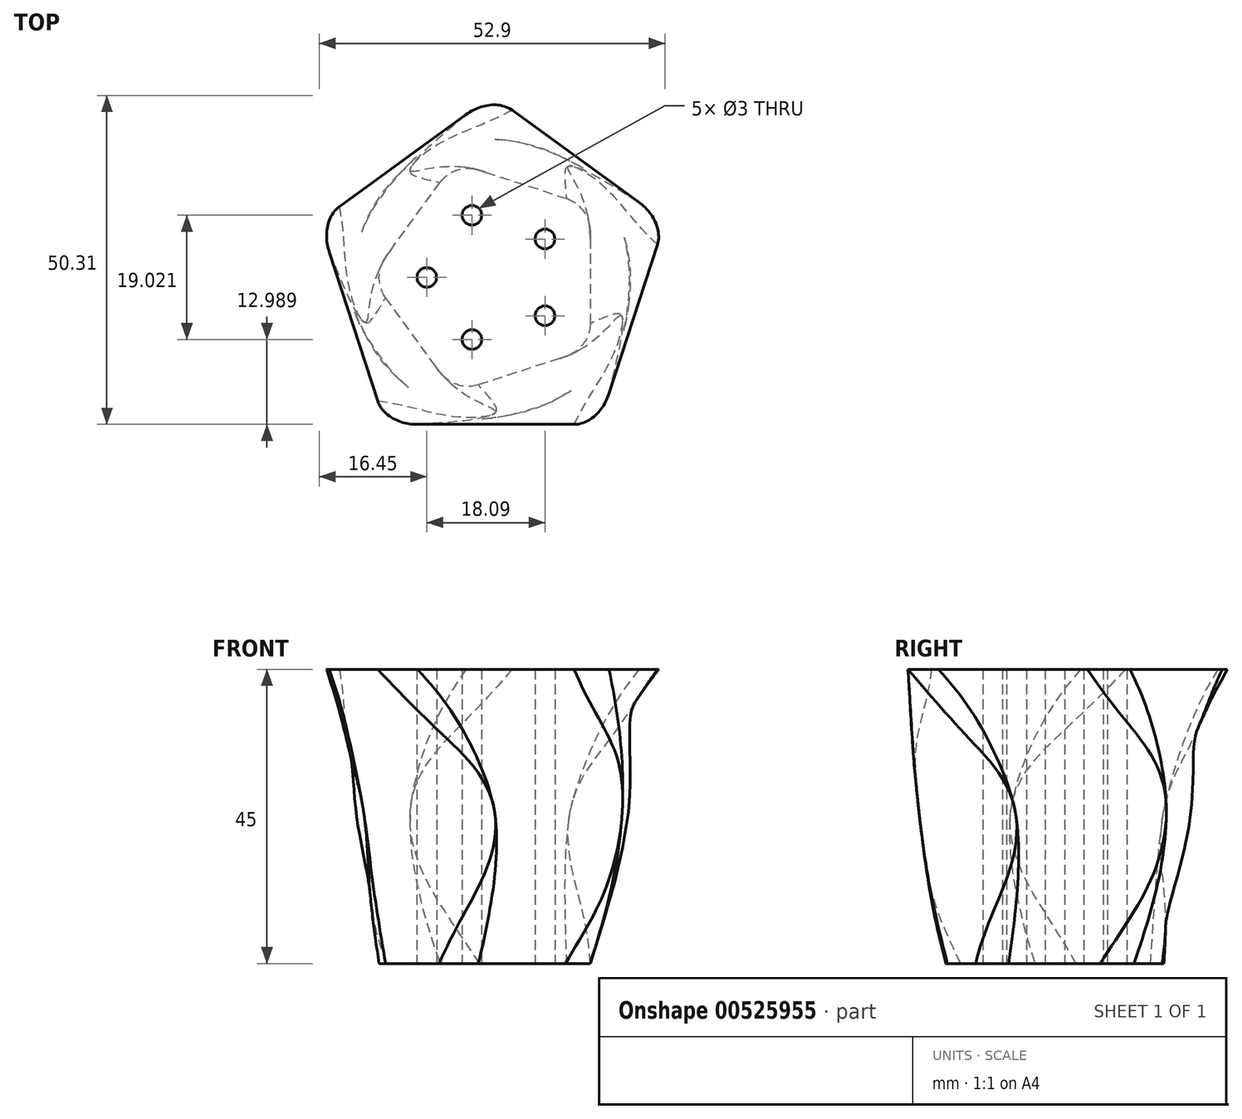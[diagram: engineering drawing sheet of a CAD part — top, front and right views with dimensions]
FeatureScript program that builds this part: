
annotation { "Feature Type Name" : "Feature", "Feature Type Description" : "" }
export const myFeature = defineFeature(function(context is Context, id is Id, definition is map)
    precondition{}
    {
        {
            var Q0;
            Q0=qCreatedBy(makeId("Top.planeOp"),FACE);
            var sketch = newSketch(context, id + "F0", { "sketchPlane" : qUnion([Q0])});
            skCircle(sketch, "E0.cCircle", {"center": v(0, 0) * mm, "radius": 15 * mm, "construction": true});
            skLineSegment(sketch, "E0.0", {"start": v(15, 10.9) * mm, "end": v(15, -10.9) * mm});
            skLineSegment(sketch, "E0.1", {"start": v(15, -10.9) * mm, "end": v(-5.73, -17.63) * mm});
            skLineSegment(sketch, "E0.2", {"start": v(-5.73, -17.63) * mm, "end": v(-18.54, 0) * mm});
            skLineSegment(sketch, "E0.3", {"start": v(-18.54, 0) * mm, "end": v(-5.73, 17.63) * mm});
            skLineSegment(sketch, "E0.4", {"start": v(-5.73, 17.63) * mm, "end": v(15, 10.9) * mm});
            skPoint(sketch, "E0.0.midPoint", {"position": v(15, 0) * mm});
            skSolve(sketch);
        }
        {
            var Q0;
            Q0=qCreatedBy(makeId("Top.planeOp"),FACE);
            cPlane(context, id + "F1", {"entities" : qUnion([Q0]), "cplaneType" : CPlaneType.OFFSET, "offset" : 25 * mm, "width" : 150 * mm, "height" : 150 * mm});
        }
        {
            var Q0;
            Q0=qCreatedBy(id+"F1.planeOp",FACE);
            var sketch = newSketch(context, id + "F2", { "sketchPlane" : qUnion([Q0])});
            skLineSegment(sketch, "E1.0", {"start": v(0, -21) * mm, "end": v(-19.97, -6.49) * mm, "construction": true});
            skLineSegment(sketch, "E1.1", {"start": v(-19.97, -6.49) * mm, "end": v(-12.34, 16.99) * mm, "construction": true});
            skLineSegment(sketch, "E1.2", {"start": v(-12.34, 16.99) * mm, "end": v(12.34, 16.99) * mm, "construction": true});
            skLineSegment(sketch, "E1.3", {"start": v(12.34, 16.99) * mm, "end": v(19.97, -6.49) * mm, "construction": true});
            skLineSegment(sketch, "E1.4", {"start": v(19.97, -6.49) * mm, "end": v(0, -21) * mm, "construction": true});
            skArc(sketch, "E2", {"start": v(19.97, -6.49) * mm, "mid": v(19.97, 6.49) * mm, "end": v(12.34, 16.99) * mm});
            skArc(sketch, "E3", {"start": v(0, -21) * mm, "mid": v(12.34, -16.99) * mm, "end": v(19.97, -6.49) * mm});
            skArc(sketch, "E4", {"start": v(-19.97, -6.49) * mm, "mid": v(-12.34, -16.99) * mm, "end": v(0, -21) * mm});
            skArc(sketch, "E5", {"start": v(-12.34, 16.99) * mm, "mid": v(-19.97, 6.49) * mm, "end": v(-19.97, -6.49) * mm});
            skArc(sketch, "E6", {"start": v(12.34, 16.99) * mm, "mid": v(0, 21) * mm, "end": v(-12.34, 16.99) * mm});
            skSolve(sketch);
        }
        {
            var Q0;
            Q0=qCreatedBy(id+"F1.planeOp",FACE);
            cPlane(context, id + "F3", {"entities" : qUnion([Q0]), "cplaneType" : CPlaneType.OFFSET, "offset" : 20 * mm, "width" : 150 * mm, "height" : 150 * mm});
        }
        {
            var Q0;
            Q0=qCreatedBy(id+"F3.planeOp",FACE);
            var sketch = newSketch(context, id + "F4", { "sketchPlane" : qUnion([Q0])});
            skCircle(sketch, "E7.cCircle", {"center": v(0, 0) * mm, "radius": 22.5 * mm, "construction": true});
            skLineSegment(sketch, "E7.0", {"start": v(16.35, -22.5) * mm, "end": v(-16.35, -22.5) * mm});
            skLineSegment(sketch, "E7.1", {"start": v(-16.35, -22.5) * mm, "end": v(-26.45, 8.6) * mm});
            skLineSegment(sketch, "E7.2", {"start": v(-26.45, 8.6) * mm, "end": v(0, 27.81) * mm});
            skLineSegment(sketch, "E7.3", {"start": v(0, 27.81) * mm, "end": v(26.45, 8.6) * mm});
            skLineSegment(sketch, "E7.4", {"start": v(26.45, 8.6) * mm, "end": v(16.35, -22.5) * mm});
            skPoint(sketch, "E7.0.midPoint", {"position": v(0, -22.5) * mm});
            skSolve(sketch);
        }
        {
            var Q0;
            Q0=makeQuery(id+"F0.imprint","IMPRINT",FACE,{"disambiguationData":[TD([[makeQuery(id+"F0.imprint","IMPRINT",EDGE,{"derivedFrom":sQuery(id+"F0.wireOp",EDGE,"E0.0")}),-1.0]])]});
            var Q1;
            Q1=makeQuery(id+"F2.imprint","IMPRINT",FACE,{"disambiguationData":[TD([[makeQuery(id+"F2.imprint","IMPRINT",EDGE,{"derivedFrom":sQuery(id+"F2.wireOp",EDGE,"E2")}),1.0]])]});
            var Q2;
            Q2=makeQuery(id+"F4.imprint","IMPRINT",FACE,{"disambiguationData":[TD([[makeQuery(id+"F4.imprint","IMPRINT",EDGE,{"derivedFrom":sQuery(id+"F4.wireOp",EDGE,"E7.0")}),-1.0]])]});
            loft(context, id + "F5", {"sheetProfilesArray" : [{ "sheetProfileEntities" : qUnion([Q0]) }, { "sheetProfileEntities" : qUnion([Q1]) }, { "sheetProfileEntities" : qUnion([Q2]) }]});
        }
        {
            var Q0;
            Q0=makeQuery(id+"F5.opLoft","SWEPT_EDGE",EDGE,{"disambiguationData":[OSD([sQuery(id+"F0.wireOp",EDGE,"E0.0"),sQuery(id+"F0.wireOp",EDGE,"E0.1"),sQuery(id+"F2.wireOp",EDGE,"E2"),sQuery(id+"F2.wireOp",EDGE,"E3"),sQuery(id+"F4.wireOp",EDGE,"E7.0"),sQuery(id+"F4.wireOp",EDGE,"E7.4")])]});
            var Q1;
            Q1=makeQuery(id+"F5.opLoft","SWEPT_EDGE",EDGE,{"disambiguationData":[OSD([sQuery(id+"F0.wireOp",EDGE,"E0.0"),sQuery(id+"F0.wireOp",EDGE,"E0.4"),sQuery(id+"F2.wireOp",EDGE,"E2"),sQuery(id+"F2.wireOp",EDGE,"E6"),sQuery(id+"F4.wireOp",EDGE,"E7.3"),sQuery(id+"F4.wireOp",EDGE,"E7.4")])]});
            var Q2;
            Q2=makeQuery(id+"F5.opLoft","SWEPT_EDGE",EDGE,{"disambiguationData":[OSD([sQuery(id+"F0.wireOp",EDGE,"E0.1"),sQuery(id+"F0.wireOp",EDGE,"E0.2"),sQuery(id+"F2.wireOp",EDGE,"E3"),sQuery(id+"F2.wireOp",EDGE,"E4"),sQuery(id+"F4.wireOp",EDGE,"E7.0"),sQuery(id+"F4.wireOp",EDGE,"E7.1")])]});
            var Q3;
            Q3=makeQuery(id+"F5.opLoft","SWEPT_EDGE",EDGE,{"disambiguationData":[OSD([sQuery(id+"F0.wireOp",EDGE,"E0.2"),sQuery(id+"F0.wireOp",EDGE,"E0.3"),sQuery(id+"F2.wireOp",EDGE,"E4"),sQuery(id+"F2.wireOp",EDGE,"E5"),sQuery(id+"F4.wireOp",EDGE,"E7.1"),sQuery(id+"F4.wireOp",EDGE,"E7.2")])]});
            var Q4;
            Q4=makeQuery(id+"F5.opLoft","SWEPT_EDGE",EDGE,{"disambiguationData":[OSD([sQuery(id+"F0.wireOp",EDGE,"E0.3"),sQuery(id+"F0.wireOp",EDGE,"E0.4"),sQuery(id+"F2.wireOp",EDGE,"E5"),sQuery(id+"F2.wireOp",EDGE,"E6"),sQuery(id+"F4.wireOp",EDGE,"E7.2"),sQuery(id+"F4.wireOp",EDGE,"E7.3")])]});
            fillet(context, id + "F6", {"entities" : qUnion([Q0, Q1, Q2, Q3, Q4]), "radius" : 5 * mm, "tangentPropagation" : true, "allowEdgeOverflow" : false});
        }
        {
            var Q0;
            Q0=makeQuery(id+"F5.opLoft","CAP_FACE",FACE,{"disambiguationData":[OSD([makeQuery(id+"F0.imprint","IMPRINT",FACE,{"disambiguationData":[TD([[makeQuery(id+"F0.imprint","IMPRINT",EDGE,{"derivedFrom":sQuery(id+"F0.wireOp",EDGE,"E0.0")}),-1.0]])]})])],"isStart":true});
            var sketch = newSketch(context, id + "F7", { "sketchPlane" : qUnion([Q0])});
            skCircle(sketch, "E8", {"center": v(-10, 0) * mm, "radius": 1.5 * mm});
            skCircle(sketch, "E9.1.0", {"center": v(-3.1, -9.51) * mm, "radius": 1.5 * mm});
            skCircle(sketch, "E9.2.0", {"center": v(8.1, -5.88) * mm, "radius": 1.5 * mm});
            skCircle(sketch, "E9.3.0", {"center": v(8.1, 5.88) * mm, "radius": 1.5 * mm});
            skCircle(sketch, "E9.4.0", {"center": v(-3.1, 9.51) * mm, "radius": 1.5 * mm});
            skPoint(sketch, "E9.center", {"position": v(0, 0) * mm});
            skSolve(sketch);
        }
        {
            var Q0;
            Q0 = qSketchRegion(id + "F7", true);
            extrude(context, id + "F8", {"entities" : qUnion([Q0]), "operationType" : NewBodyOperationType.REMOVE, "endBound" : BoundingType.THROUGH_ALL, "oppositeDirection" : true, "depth" : 25 * mm, "offsetDistance" : 25 * mm});
        }
    });
